FCSTD DOCUMENT  (FreeCAD 0.18.2R)
Label: JACK
License: All rights reserved
LicenseURL: http://en.wikipedia.org/wiki/All_rights_reserved
objects: App::DocumentObjectGroupPython×9, Part::Cylinder×8, Part::FeaturePython×6, Part::Cut×4, Part::Compound×3, Part::Feature×3, Part::Box×2, Part::Chamfer×2, Part::Fillet×1, Part::MultiFuse×1
note: 30 computed .brp shape members not serialized (recipe doc carries the construction recipe); baked Part::Feature solids carry a one-line shape summary decoded from their .brp

FEATURE [Part::Box] Box  label="Cube"
  AttacherType = Attacher::AttachEngine3D
  Height = 30
  Length = 50
  Placement = pos=(-25,-25,-15) rot=(0,0,1;0rad)
  Width = 50
FEATURE [Part::Cylinder] Cylinder
  Angle = 360
  AttacherType = Attacher::AttachEngine3D
  Height = 100
  Placement = pos=(-15,45,-1e-14) rot=(1,0,0;1.5708rad)
  Radius = 5
FEATURE [Part::Cylinder] Cylinder001
  Angle = 360
  AttacherType = Attacher::AttachEngine3D
  Height = 100
  Placement = pos=(15,45,-1e-14) rot=(1,0,0;1.5708rad)
  Radius = 5
FEATURE [Part::Compound] Compound
  Links = -> [Cylinder001,Cylinder]
FEATURE [Part::Cut] Cut
  Base = -> Box
  Tool = -> Compound
FEATURE [Part::Feature] Cut001  label="FIXED BASE"
  Placement = pos=(-15,0,0) rot=(0,0,1;0rad)
  shape: bbox 50 x 50 x 30 mm, 8 faces (baked)
FEATURE [Part::Feature] Cut001001  label="MOBILE BASE"
  Placement = pos=(-15,0,193.831) rot=(0,0,1;0rad)
  shape: bbox 50 x 50 x 30 mm, 8 faces (baked)
FEATURE [Part::Feature] Cut001002
  shape: bbox 50 x 50 x 30 mm, 8 faces (baked)
FEATURE [Part::Cylinder] Cylinder002
  Angle = 360
  AttacherType = Attacher::AttachEngine3D
  Height = 100
  Placement = pos=(0,0,-60) rot=(0,0,1;0rad)
  Radius = 8
FEATURE [Part::Cut] Cut001003  label="RIGHT JOINT"
  Base = -> Cut001002
  Placement = pos=(125.658,0,96.9153) rot=(0,1,0;1.5708rad)
  Tool = -> Cylinder002
FEATURE [Part::FeaturePython] ThreadedRod  label="M16x100.0-ThreadedRod"  # Fasteners workbench fastener (typed FeaturePython)
  Placement = pos=(0,0,50) rot=(0,0,1;0rad)
  diameter = 13
  invert = false
  length = 100
  matchOuter = false
  offset = 0
  thread = true
FEATURE [Part::Cut] Cut001004  label="LEFT JOINT"
  Base = -> Cut
  Placement = pos=(-155.658,0,96.9153) rot=(0,1,0;1.5708rad)
  Tool = -> ThreadedRod
FEATURE [Part::Box] Box001  label="Cube001"
  AttacherType = Attacher::AttachEngine3D
  Height = 20
  Length = 170
  Placement = pos=(-10,-10,-10) rot=(0,0,1;0rad)
  Width = 5
FEATURE [Part::Cylinder] Cylinder003
  Angle = 360
  AttacherType = Attacher::AttachEngine3D
  Height = 10
  Placement = pos=(0,0,0) rot=(1,0,0;1.5708rad)
  Radius = 5
FEATURE [Part::Cylinder] Cylinder004
  Angle = 360
  AttacherType = Attacher::AttachEngine3D
  Height = 10
  Placement = pos=(150,0,0) rot=(1,0,0;1.5708rad)
  Radius = 5
FEATURE [Part::Fillet] Fillet
  Base = -> Box001
  Edges = 4 edges r=8: [Edge2,Edge4,Edge6,Edge8]
FEATURE [Part::Compound] Compound001
  Links = -> [Cylinder004,Cylinder003]
FEATURE [Part::Cut] Cut001005
  Base = -> Fillet
  Placement = pos=(0,-20,0) rot=(0,0,1;0rad)
  Tool = -> Compound001
FEATURE [Part::FeaturePython] Clone  label="Cut001006"  # Draft clone (typed FeaturePython)
  AttacherType = Attacher::AttachEngine3D
  Fuse = false
  Objects = -> [Cut001005]
  Placement = pos=(0,35,0) rot=(0,0,1;0rad)
  Scale = (1,1,1)
FEATURE [Part::Compound] Compound002  label="ARM_1"
  Links = -> [Clone,Cut001005]
  Placement = pos=(0,0,0) rot=(0,1,0;5.70548rad)
FEATURE [Part::FeaturePython] Clone001  label="ARM_002"  # Draft clone (typed FeaturePython)
  AttacherType = Attacher::AttachEngine3D
  Fuse = false
  Objects = -> [Compound002]
  Placement = pos=(-30,0,0) rot=(0,1,0;3.7193rad)
  Scale = (1,1,1)
FEATURE [Part::FeaturePython] Clone002  label="ARM_003"  # Draft clone (typed FeaturePython)
  AttacherType = Attacher::AttachEngine3D
  Fuse = false
  Objects = -> [Clone001]
  Placement = pos=(125.658,0,111.915) rot=(0,1,0;3.7193rad)
  Scale = (1,1,1)
FEATURE [Part::FeaturePython] Clone003  label="ARM_004"  # Draft clone (typed FeaturePython)
  AttacherType = Attacher::AttachEngine3D
  Fuse = false
  Objects = -> [Clone002]
  Placement = pos=(-155.658,0,111.915) rot=(0,1,0;5.70548rad)
  Scale = (1,1,1)
FEATURE [Part::FeaturePython] ThreadedRod001  label="M16x330.0-ThreadedRod"  # Fasteners workbench fastener (typed FeaturePython)
  Placement = pos=(-50,0,-1.11e-14) rot=(0,1,0;1.5708rad)
  diameter = 13
  invert = false
  length = 330
  matchOuter = false
  offset = 0
  thread = true
FEATURE [Part::Cylinder] Cylinder005
  Angle = 360
  AttacherType = Attacher::AttachEngine3D
  Height = 50
  Placement = pos=(0,0,0) rot=(0,-1,0;1.5708rad)
  Radius = 8
FEATURE [Part::Cylinder] Cylinder006
  Angle = 360
  AttacherType = Attacher::AttachEngine3D
  Height = 25
  Placement = pos=(0,0,0) rot=(0,1,0;1.5708rad)
  Radius = 10
FEATURE [Part::Cylinder] Cylinder007
  Angle = 360
  AttacherType = Attacher::AttachEngine3D
  Height = 200
  Placement = pos=(15,100,-2.22e-14) rot=(1,0,0;1.5708rad)
  Radius = 5
FEATURE [Part::Chamfer] Chamfer
  Base = -> Cylinder006
  Edges = 1 edges r=2: [Edge1]
FEATURE [Part::Chamfer] Chamfer001
  Base = -> Cylinder007
  Edges = 2 edges r=1: [Edge1,Edge3]
FEATURE [Part::MultiFuse] Fusion  label="SHAFT"
  Placement = pos=(140.658,0,96.9153) rot=(1,0,0;0.523599rad)
  Shapes = -> [Chamfer001,Chamfer,Cylinder005,ThreadedRod001]
FEATURE [App::DocumentObjectGroupPython] My_Placer  # scripted group (container) (typed FeaturePython)
  Placement = pos=(-15,0,193.831) rot=(0,0,1;0rad)
  RotAxis = (0,0,1)
  RotCenter = (0,0,0)
  arc = 0
  arc0 = 0
  arc1 = 90
  target = -> Cut001001
  time = 0.33
  x = -15
  x0 = 0
  x1 = 0.546102
  y = 0
  y0 = 0
  y1 = 0
  z = 150*x1*2+30
  z0 = 0
  z1 = 0
  expr: x1 = sin(time * 70 + 10)
FEATURE [App::DocumentObjectGroupPython] My_Placer001  # scripted group (container) (typed FeaturePython)
  Placement = pos=(125.658,0,96.9153) rot=(0,1,0;1.5708rad)
  RotAxis = (0,1,0)
  RotCenter = (0,0,0)
  arc = 90
  arc0 = 0
  arc1 = 90
  target = -> Cut001003
  time = 0.33
  x = 150*x0
  x0 = 0.837719
  x1 = 0.546102
  y = 0
  y0 = 0
  y1 = 0
  z = 15+150*x1
  z0 = 0
  z1 = 0
  expr: x1 = sin(time * 70 + 10)
  expr: x0 = cos(time * 70 + 10)
FEATURE [App::DocumentObjectGroupPython] My_Placer002  # scripted group (container) (typed FeaturePython)
  Placement = pos=(-155.658,0,96.9153) rot=(0,1,0;1.5708rad)
  RotAxis = (0,1,0)
  RotCenter = (0,0,0)
  arc = 90
  arc0 = 0
  arc1 = 90
  target = -> Cut001004
  time = 0.33
  x =  -150*x0-30
  x0 = 0.837719
  x1 = 0.546102
  y = 0
  y0 = 0
  y1 = 0
  z = 15+150*x1
  z0 = 0
  z1 = 0
  expr: x1 = sin(time * 70 + 10)
  expr: x0 = cos(time * 70 + 10)
FEATURE [App::DocumentObjectGroupPython] My_Placer003  # scripted group (container) (typed FeaturePython)
  Placement = pos=(0,0,0) rot=(0,1,0;-0.577704rad)
  RotAxis = (0,1,0)
  RotCenter = (0,0,0)
  arc =  -time*70-10
  arc0 = 0
  arc1 = 90
  target = -> Compound002
  time = 0.33
  x = 0
  x0 = 0
  x1 = 200
  y = 0
  y0 = 0
  y1 = 0
  z = 0
  z0 = 0
  z1 = 0
FEATURE [App::DocumentObjectGroupPython] My_Placer004  # scripted group (container) (typed FeaturePython)
  Placement = pos=(-30,0,0) rot=(0,1,0;3.7193rad)
  RotAxis = (0,1,0)
  RotCenter = (0,0,0)
  arc = 190+time*70
  arc0 = 0
  arc1 = 90
  target = -> Clone001
  time = 0.33
  x = -30
  x0 = 0
  x1 = 200
  y = 0
  y0 = 0
  y1 = 0
  z = 0
  z0 = 0
  z1 = 0
FEATURE [App::DocumentObjectGroupPython] My_Placer005  # scripted group (container) (typed FeaturePython)
  Placement = pos=(125.658,0,111.915) rot=(0,1,0;3.7193rad)
  RotAxis = (0,1,0)
  RotCenter = (0,0,0)
  arc = 190+time*70
  arc0 = 0
  arc1 = 90
  target = -> Clone002
  time = 0.33
  x = 150*x0
  x0 = 0.837719
  x1 = 0.546102
  y = 0
  y0 = 0
  y1 = 0
  z = 30+150*x1
  z0 = 0
  z1 = 0
  expr: x1 = sin(time * 70 + 10)
  expr: x0 = cos(time * 70 + 10)
FEATURE [App::DocumentObjectGroupPython] My_Placer006  # scripted group (container) (typed FeaturePython)
  Placement = pos=(-155.658,0,111.915) rot=(0,1,0;5.70548rad)
  RotAxis = (0,1,0)
  RotCenter = (0,0,0)
  arc = 350-time*70
  arc0 = 0
  arc1 = 90
  target = -> Clone003
  time = 0.33
  x = -150*x0-30
  x0 = 0.837719
  x1 = 0.546102
  y = 0
  y0 = 0
  y1 = 0
  z = 30+150*x1
  z0 = 0
  z1 = 0
  expr: x1 = sin(time * 70 + 10)
  expr: x0 = cos(time * 70 + 10)
FEATURE [App::DocumentObjectGroupPython] My_Placer007  # scripted group (container) (typed FeaturePython)
  Placement = pos=(140.658,0,96.9153) rot=(1,0,0;-5.75959rad)
  RotAxis = (1,0,0)
  RotCenter = (0,0,0)
  arc = -time*1000
  arc0 = 0
  arc1 = 90
  target = -> Fusion
  time = 0.33
  x = 150*x0+15
  x0 = 0.837719
  x1 = 0.546102
  y = 0
  y0 = 0
  y1 = 0
  z = 15+150*x1
  z0 = 0
  z1 = 0
  expr: x1 = sin(time * 70 + 10)
  expr: x0 = cos(time * 70 + 10)
FEATURE [App::DocumentObjectGroupPython] My_Manager  # scripted group (container) (typed FeaturePython)
  Group = -> [My_Placer,My_Placer001,My_Placer002,My_Placer003,My_Placer004,My_Placer005,My_Placer006,My_Placer007]
  intervall = 100
  sleeptime = 0.02
  start = 0
  step = 33
  text = NO
